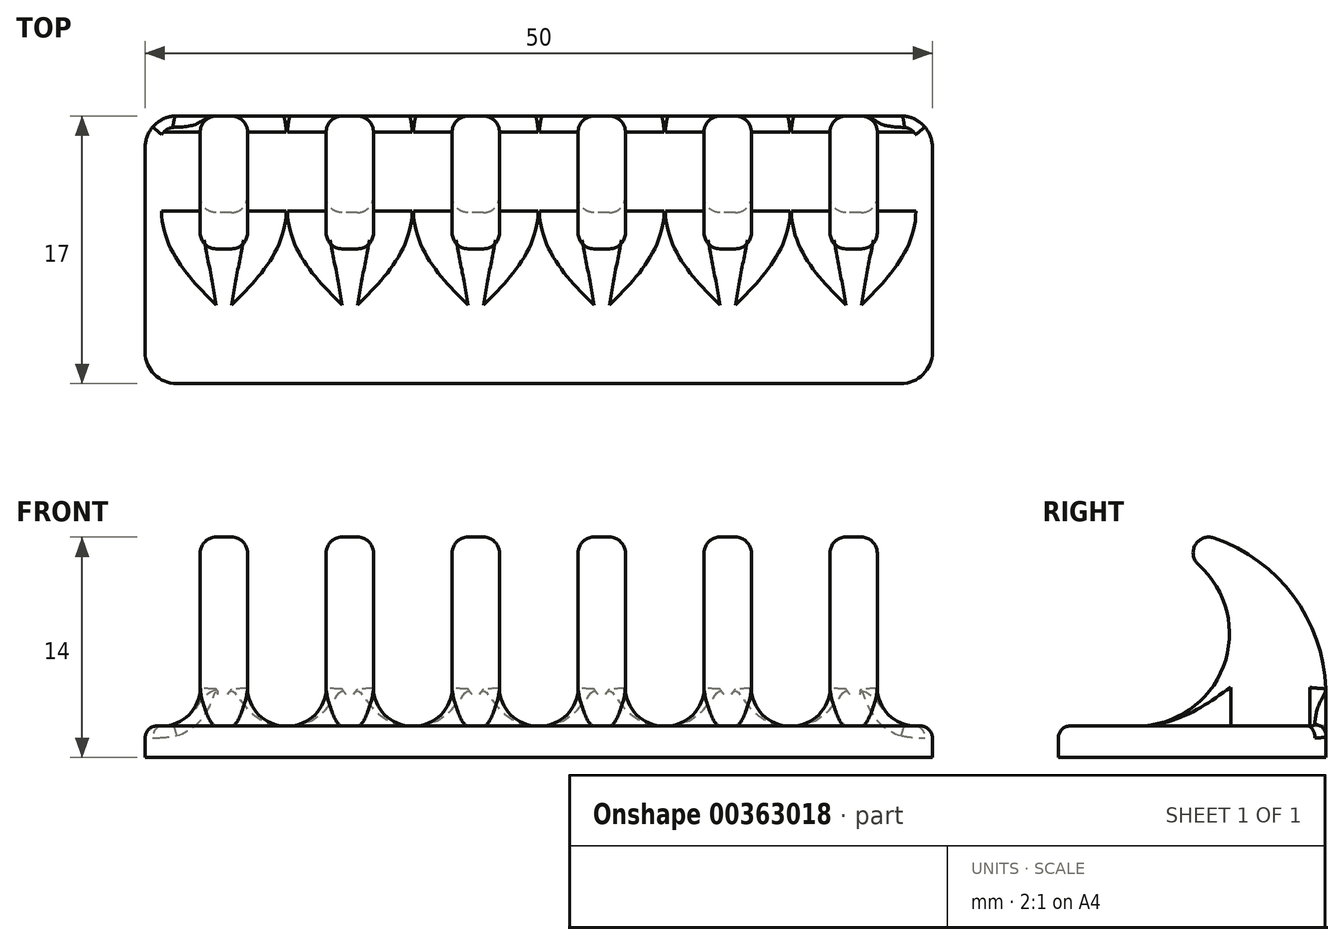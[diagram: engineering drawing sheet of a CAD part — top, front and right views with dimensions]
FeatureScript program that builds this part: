
annotation { "Feature Type Name" : "Feature", "Feature Type Description" : "" }
export const myFeature = defineFeature(function(context is Context, id is Id, definition is map)
    precondition{}
    {
        {
            var Q0;
            Q0=qCreatedBy(makeId("Top.planeOp"),FACE);
            var sketch = newSketch(context, id + "F0", { "sketchPlane" : qUnion([Q0])});
            skLineSegment(sketch, "E0.bottom", {"start": v(0, 0) * mm, "end": v(50, 0) * mm});
            skLineSegment(sketch, "E0.top", {"start": v(0, 17) * mm, "end": v(50, 17) * mm});
            skLineSegment(sketch, "E0.left", {"start": v(0, 0) * mm, "end": v(0, 17) * mm});
            skLineSegment(sketch, "E0.right", {"start": v(50, 0) * mm, "end": v(50, 17) * mm});
            skSolve(sketch);
        }
        {
            var Q0;
            Q0 = qSketchRegion(id + "F0", true);
            extrude(context, id + "F1", {"entities" : qUnion([Q0]), "depth" : 2 * mm});
        }
        {
            var Q0;
            Q0=makeQuery(id+"F1.opExtrude","CAP_FACE",FACE,{"disambiguationData":[OSD([sQuery(id+"F0.wireOp",EDGE,"E0.bottom"),sQuery(id+"F0.wireOp",EDGE,"E0.top"),sQuery(id+"F0.wireOp",EDGE,"E0.left"),sQuery(id+"F0.wireOp",EDGE,"E0.right")])],"isStart":false});
            var sketch = newSketch(context, id + "F2", { "sketchPlane" : qUnion([Q0])});
            skPoint(sketch, "E1", {"position": v(25, 17) * mm});
            skSolve(sketch);
        }
        {
            var Q0;
            Q0=makeQuery(id+"F1.opExtrude","CAP_EDGE",EDGE,{"disambiguationData":[OSD([sQuery(id+"F0.wireOp",EDGE,"E0.top")])],"isStart":false});
            cPoint(context, id + "F3", {"entities" : qUnion([Q0]), "parameter" : 0.5});
        }
        {
            var Q0;
            Q0 = qCreatedBy(id + "F3" ,VERTEX);
            var Q1;
            Q1=qCreatedBy(makeId("Right.planeOp"),FACE);
            cPlane(context, id + "F4", {"entities" : qUnion([Q0, Q1]), "cplaneType" : CPlaneType.PLANE_POINT, "offset" : 25 * mm, "width" : 150 * mm, "height" : 150 * mm});
        }
        {
            var Q0;
            Q0=qCreatedBy(id+"F4.planeOp",FACE);
            var sketch = newSketch(context, id + "F5", { "sketchPlane" : qUnion([Q0])});
            skLineSegment(sketch, "E2", {"start": v(5, 2) * mm, "end": v(17, 2) * mm});
            skArc(sketch, "E3", {"start": v(9.89, 13.95) * mm, "mid": v(8.7, 13.5) * mm, "end": v(8.9, 12.25) * mm});
            skLineSegment(sketch, "E4", {"start": v(17, 2) * mm, "end": v(17, 4) * mm});
            skArc(sketch, "E5", {"start": v(17, 4) * mm, "mid": v(15.04, 10.11) * mm, "end": v(9.89, 13.95) * mm});
            skLineSegment(sketch, "E6", {"start": v(8.9, 12.25) * mm, "end": v(8.9, 12.25) * mm});
            skArc(sketch, "E7", {"start": v(8.9, 12.25) * mm, "mid": v(10.48, 5.78) * mm, "end": v(5, 2) * mm});
            skSolve(sketch);
        }
        {
            var Q0;
            Q0 = qSketchRegion(id + "F5", true);
            extrude(context, id + "F6", {"entities" : qUnion([Q0]), "operationType" : NewBodyOperationType.ADD, "endBound" : BoundingType.SYMMETRIC, "depth" : 50 * mm});
        }
        {
            var Q0;
            Q0=makeQuery(id+"F1.opExtrude","SWEPT_FACE",FACE,{"disambiguationData":[OSD([sQuery(id+"F0.wireOp",EDGE,"E0.top")])]});
            var sketch = newSketch(context, id + "F7", { "sketchPlane" : qUnion([Q0])});
            skLineSegment(sketch, "E8.bottom", {"start": v(-27.5, 2) * mm, "end": v(-22.5, 2) * mm});
            skLineSegment(sketch, "E8.top", {"start": v(-27.5, 19) * mm, "end": v(-22.5, 19) * mm});
            skLineSegment(sketch, "E8.left", {"start": v(-27.5, 2) * mm, "end": v(-27.5, 19) * mm});
            skLineSegment(sketch, "E8.right", {"start": v(-22.5, 2) * mm, "end": v(-22.5, 19) * mm});
            skLineSegment(sketch, "E9.bottom", {"start": v(-6.5, 2) * mm, "end": v(-11.5, 2) * mm});
            skLineSegment(sketch, "E9.top", {"start": v(-6.5, 19) * mm, "end": v(-11.5, 19) * mm});
            skLineSegment(sketch, "E9.left", {"start": v(-6.5, 2) * mm, "end": v(-6.5, 19) * mm});
            skLineSegment(sketch, "E9.right", {"start": v(-11.5, 2) * mm, "end": v(-11.5, 19) * mm});
            skPoint(sketch, "E10", {"position": v(-9, 19) * mm});
            skLineSegment(sketch, "E11.bottom", {"start": v(8.53, 2) * mm, "end": v(-3.5, 2) * mm});
            skLineSegment(sketch, "E11.top", {"start": v(8.53, 19) * mm, "end": v(-3.5, 19) * mm});
            skLineSegment(sketch, "E11.left", {"start": v(8.53, 2) * mm, "end": v(8.53, 19) * mm});
            skLineSegment(sketch, "E11.right", {"start": v(-3.5, 2) * mm, "end": v(-3.5, 19) * mm});
            skPoint(sketch, "E12.firstSnap0", {"position": v(-25, 2) * mm});
            skLineSegment(sketch, "E12.bottom", {"start": v(-19.5, 2) * mm, "end": v(-14.5, 2) * mm});
            skLineSegment(sketch, "E12.top", {"start": v(-19.5, 19) * mm, "end": v(-14.5, 19) * mm});
            skLineSegment(sketch, "E12.left", {"start": v(-19.5, 2) * mm, "end": v(-19.5, 19) * mm});
            skLineSegment(sketch, "E12.right", {"start": v(-14.5, 2) * mm, "end": v(-14.5, 19) * mm});
            skLineSegment(sketch, "E13", {"start": v(-25, 2) * mm, "end": v(-25, -6.71) * mm, "construction": true});
            skPoint(sketch, "E13.endSnap0", {"position": v(-25, 0) * mm});
            skLineSegment(sketch, "E14.MirrorCS", {"start": v(-38.5, 2) * mm, "end": v(-38.5, 19) * mm});
            skLineSegment(sketch, "E15.MirrorCS", {"start": v(-58.53, 2) * mm, "end": v(-46.5, 2) * mm});
            skLineSegment(sketch, "E16.MirrorCS", {"start": v(-58.53, 19) * mm, "end": v(-46.5, 19) * mm});
            skLineSegment(sketch, "E17.MirrorCS", {"start": v(-58.53, 2) * mm, "end": v(-58.53, 19) * mm});
            skLineSegment(sketch, "E18.MirrorCS", {"start": v(-46.5, 2) * mm, "end": v(-46.5, 19) * mm});
            skLineSegment(sketch, "E19.MirrorCS", {"start": v(-30.5, 19) * mm, "end": v(-35.5, 19) * mm});
            skLineSegment(sketch, "E20.MirrorCS", {"start": v(-43.5, 2) * mm, "end": v(-43.5, 19) * mm});
            skLineSegment(sketch, "E21.MirrorCS", {"start": v(-35.5, 2) * mm, "end": v(-35.5, 19) * mm});
            skLineSegment(sketch, "E22.MirrorCS", {"start": v(-30.5, 2) * mm, "end": v(-30.5, 19) * mm});
            skPoint(sketch, "E23.MirrorP", {"position": v(-41, 19) * mm});
            skLineSegment(sketch, "E24.MirrorCS", {"start": v(-43.5, 19) * mm, "end": v(-38.5, 19) * mm});
            skLineSegment(sketch, "E25.MirrorCS", {"start": v(-43.5, 2) * mm, "end": v(-38.5, 2) * mm});
            skLineSegment(sketch, "E26.MirrorCS", {"start": v(-30.5, 2) * mm, "end": v(-35.5, 2) * mm});
            skSolve(sketch);
        }
        {
            var Q0;
            Q0 = qSketchRegion(id + "F7", true);
            extrude(context, id + "F8", {"entities" : qUnion([Q0]), "operationType" : NewBodyOperationType.REMOVE, "oppositeDirection" : true, "depth" : 25 * mm});
        }
        {
            var Q0;
            Q0=makeQuery(id+"F6.opExtrude","CAP_EDGE",EDGE,{"disambiguationData":[OSD([sQuery(id+"F5.wireOp",EDGE,"E5")])],"isStart":true});
            var Q1;
            Q1=makeQuery(id+"F8.boolean.opBoolean","INTERSECT",EDGE,{"derivedFrom":[makeQuery(id+"F6.opExtrude","SWEPT_FACE",FACE,{"disambiguationData":[OSD([sQuery(id+"F5.wireOp",EDGE,"E5")])]}),makeQuery(id+"F8.opExtrude","SWEPT_FACE",FACE,{"disambiguationData":[OSD([sQuery(id+"F7.wireOp",EDGE,"E8.right")])]})]});
            var Q2;
            Q2=makeQuery(id+"F8.boolean.opBoolean","INTERSECT",EDGE,{"derivedFrom":[makeQuery(id+"F6.opExtrude","SWEPT_FACE",FACE,{"disambiguationData":[OSD([sQuery(id+"F5.wireOp",EDGE,"E5")])]}),makeQuery(id+"F8.opExtrude","SWEPT_FACE",FACE,{"disambiguationData":[OSD([sQuery(id+"F7.wireOp",EDGE,"E12.right")])]})]});
            var Q3;
            Q3=makeQuery(id+"F8.boolean.opBoolean","INTERSECT",EDGE,{"derivedFrom":[makeQuery(id+"F6.opExtrude","SWEPT_FACE",FACE,{"disambiguationData":[OSD([sQuery(id+"F5.wireOp",EDGE,"E5")])]}),makeQuery(id+"F8.opExtrude","SWEPT_FACE",FACE,{"disambiguationData":[OSD([sQuery(id+"F7.wireOp",EDGE,"E9.left")])]})]});
            var Q4;
            Q4=makeQuery(id+"F8.boolean.opBoolean","INTERSECT",EDGE,{"derivedFrom":[makeQuery(id+"F6.opExtrude","SWEPT_FACE",FACE,{"disambiguationData":[OSD([sQuery(id+"F5.wireOp",EDGE,"E5")])]}),makeQuery(id+"F8.opExtrude","SWEPT_FACE",FACE,{"disambiguationData":[OSD([sQuery(id+"F7.wireOp",EDGE,"E22.MirrorCS")])]})]});
            var Q5;
            Q5=makeQuery(id+"F8.boolean.opBoolean","INTERSECT",EDGE,{"derivedFrom":[makeQuery(id+"F6.opExtrude","SWEPT_FACE",FACE,{"disambiguationData":[OSD([sQuery(id+"F5.wireOp",EDGE,"E5")])]}),makeQuery(id+"F8.opExtrude","SWEPT_FACE",FACE,{"disambiguationData":[OSD([sQuery(id+"F7.wireOp",EDGE,"E14.MirrorCS")])]})]});
            var Q6;
            Q6=makeQuery(id+"F8.boolean.opBoolean","INTERSECT",EDGE,{"derivedFrom":[makeQuery(id+"F6.opExtrude","SWEPT_FACE",FACE,{"disambiguationData":[OSD([sQuery(id+"F5.wireOp",EDGE,"E5")])]}),makeQuery(id+"F8.opExtrude","SWEPT_FACE",FACE,{"disambiguationData":[OSD([sQuery(id+"F7.wireOp",EDGE,"E18.MirrorCS")])]})]});
            fillet(context, id + "F9", {"entities" : qUnion([Q0, Q1, Q2, Q3, Q4, Q5, Q6]), "radius" : 1 * mm, "tangentPropagation" : true, "allowEdgeOverflow" : false});
        }
        {
            var Q0;
            Q0=makeQuery(id+"F6.opExtrude","CAP_EDGE",EDGE,{"disambiguationData":[OSD([sQuery(id+"F5.wireOp",EDGE,"E5")])],"isStart":false});
            var Q1;
            Q1=makeQuery(id+"F8.boolean.opBoolean","INTERSECT",EDGE,{"derivedFrom":[makeQuery(id+"F6.opExtrude","SWEPT_FACE",FACE,{"disambiguationData":[OSD([sQuery(id+"F5.wireOp",EDGE,"E5")])]}),makeQuery(id+"F8.opExtrude","SWEPT_FACE",FACE,{"disambiguationData":[OSD([sQuery(id+"F7.wireOp",EDGE,"E8.left")])]})]});
            var Q2;
            Q2=makeQuery(id+"F8.boolean.opBoolean","INTERSECT",EDGE,{"derivedFrom":[makeQuery(id+"F6.opExtrude","SWEPT_FACE",FACE,{"disambiguationData":[OSD([sQuery(id+"F5.wireOp",EDGE,"E5")])]}),makeQuery(id+"F8.opExtrude","SWEPT_FACE",FACE,{"disambiguationData":[OSD([sQuery(id+"F7.wireOp",EDGE,"E20.MirrorCS")])]})]});
            var Q3;
            Q3=makeQuery(id+"F8.boolean.opBoolean","INTERSECT",EDGE,{"derivedFrom":[makeQuery(id+"F6.opExtrude","SWEPT_FACE",FACE,{"disambiguationData":[OSD([sQuery(id+"F5.wireOp",EDGE,"E5")])]}),makeQuery(id+"F8.opExtrude","SWEPT_FACE",FACE,{"disambiguationData":[OSD([sQuery(id+"F7.wireOp",EDGE,"E21.MirrorCS")])]})]});
            var Q4;
            Q4=makeQuery(id+"F8.boolean.opBoolean","INTERSECT",EDGE,{"derivedFrom":[makeQuery(id+"F6.opExtrude","SWEPT_FACE",FACE,{"disambiguationData":[OSD([sQuery(id+"F5.wireOp",EDGE,"E5")])]}),makeQuery(id+"F8.opExtrude","SWEPT_FACE",FACE,{"disambiguationData":[OSD([sQuery(id+"F7.wireOp",EDGE,"E12.left")])]})]});
            var Q5;
            Q5=makeQuery(id+"F8.boolean.opBoolean","INTERSECT",EDGE,{"derivedFrom":[makeQuery(id+"F6.opExtrude","SWEPT_FACE",FACE,{"disambiguationData":[OSD([sQuery(id+"F5.wireOp",EDGE,"E5")])]}),makeQuery(id+"F8.opExtrude","SWEPT_FACE",FACE,{"disambiguationData":[OSD([sQuery(id+"F7.wireOp",EDGE,"E9.right")])]})]});
            var Q6;
            Q6=makeQuery(id+"F8.boolean.opBoolean","INTERSECT",EDGE,{"derivedFrom":[makeQuery(id+"F6.opExtrude","SWEPT_FACE",FACE,{"disambiguationData":[OSD([sQuery(id+"F5.wireOp",EDGE,"E5")])]}),makeQuery(id+"F8.opExtrude","SWEPT_FACE",FACE,{"disambiguationData":[OSD([sQuery(id+"F7.wireOp",EDGE,"E11.right")])]})]});
            fillet(context, id + "F10", {"entities" : qUnion([Q0, Q1, Q2, Q3, Q4, Q5, Q6]), "radius" : 1 * mm, "tangentPropagation" : true, "allowEdgeOverflow" : false});
        }
        {
            var Q0;
            Q0=makeQuery(id+"F6.opExtrude","CAP_EDGE",EDGE,{"disambiguationData":[OSD([sQuery(id+"F5.wireOp",EDGE,"E2")])],"isStart":false});
            var Q1;
            Q1=makeQuery(id+"F8.boolean.opBoolean","COPY",EDGE,{"derivedFrom":makeQuery(id+"F8.opExtrude","SWEPT_EDGE",EDGE,{"disambiguationData":[OSD([sQuery(id+"F7.wireOp",EDGE,"E8.bottom"),sQuery(id+"F7.wireOp",EDGE,"E8.left")])]})});
            var Q2;
            Q2=makeQuery(id+"F8.boolean.opBoolean","COPY",EDGE,{"derivedFrom":makeQuery(id+"F8.opExtrude","SWEPT_EDGE",EDGE,{"disambiguationData":[OSD([sQuery(id+"F7.wireOp",EDGE,"E20.MirrorCS"),sQuery(id+"F7.wireOp",EDGE,"E25.MirrorCS")])]})});
            var Q3;
            Q3=makeQuery(id+"F8.boolean.opBoolean","COPY",EDGE,{"derivedFrom":makeQuery(id+"F8.opExtrude","SWEPT_EDGE",EDGE,{"disambiguationData":[OSD([sQuery(id+"F7.wireOp",EDGE,"E21.MirrorCS"),sQuery(id+"F7.wireOp",EDGE,"E26.MirrorCS")])]})});
            var Q4;
            Q4=makeQuery(id+"F8.boolean.opBoolean","COPY",EDGE,{"derivedFrom":makeQuery(id+"F8.opExtrude","SWEPT_EDGE",EDGE,{"disambiguationData":[OSD([sQuery(id+"F7.wireOp",EDGE,"E12.bottom"),sQuery(id+"F7.wireOp",EDGE,"E12.left")])]})});
            var Q5;
            Q5=makeQuery(id+"F8.boolean.opBoolean","COPY",EDGE,{"derivedFrom":makeQuery(id+"F8.opExtrude","SWEPT_EDGE",EDGE,{"disambiguationData":[OSD([sQuery(id+"F7.wireOp",EDGE,"E9.bottom"),sQuery(id+"F7.wireOp",EDGE,"E9.right")])]})});
            var Q6;
            Q6=makeQuery(id+"F8.boolean.opBoolean","COPY",EDGE,{"derivedFrom":makeQuery(id+"F8.opExtrude","SWEPT_EDGE",EDGE,{"disambiguationData":[OSD([sQuery(id+"F7.wireOp",EDGE,"E11.bottom"),sQuery(id+"F7.wireOp",EDGE,"E11.right")])]})});
            fillet(context, id + "F11", {"entities" : qUnion([Q0, Q1, Q2, Q3, Q4, Q5, Q6]), "radius" : 2.45 * mm, "tangentPropagation" : true, "allowEdgeOverflow" : false});
        }
        {
            var Q0;
            Q0=makeQuery(id+"F8.boolean.opBoolean","COPY",EDGE,{"derivedFrom":makeQuery(id+"F8.opExtrude","SWEPT_EDGE",EDGE,{"disambiguationData":[OSD([sQuery(id+"F7.wireOp",EDGE,"E8.bottom"),sQuery(id+"F7.wireOp",EDGE,"E8.right")])]})});
            var Q1;
            Q1=makeQuery(id+"F6.opExtrude","CAP_EDGE",EDGE,{"disambiguationData":[OSD([sQuery(id+"F5.wireOp",EDGE,"E2")])],"isStart":true});
            var Q2;
            Q2=makeQuery(id+"F8.boolean.opBoolean","COPY",EDGE,{"derivedFrom":makeQuery(id+"F8.opExtrude","SWEPT_EDGE",EDGE,{"disambiguationData":[OSD([sQuery(id+"F7.wireOp",EDGE,"E9.bottom"),sQuery(id+"F7.wireOp",EDGE,"E9.left")])]})});
            var Q3;
            Q3=makeQuery(id+"F8.boolean.opBoolean","COPY",EDGE,{"derivedFrom":makeQuery(id+"F8.opExtrude","SWEPT_EDGE",EDGE,{"disambiguationData":[OSD([sQuery(id+"F7.wireOp",EDGE,"E12.bottom"),sQuery(id+"F7.wireOp",EDGE,"E12.right")])]})});
            var Q4;
            Q4=makeQuery(id+"F8.boolean.opBoolean","COPY",EDGE,{"derivedFrom":makeQuery(id+"F8.opExtrude","SWEPT_EDGE",EDGE,{"disambiguationData":[OSD([sQuery(id+"F7.wireOp",EDGE,"E22.MirrorCS"),sQuery(id+"F7.wireOp",EDGE,"E26.MirrorCS")])]})});
            var Q5;
            Q5=makeQuery(id+"F8.boolean.opBoolean","COPY",EDGE,{"derivedFrom":makeQuery(id+"F8.opExtrude","SWEPT_EDGE",EDGE,{"disambiguationData":[OSD([sQuery(id+"F7.wireOp",EDGE,"E14.MirrorCS"),sQuery(id+"F7.wireOp",EDGE,"E25.MirrorCS")])]})});
            var Q6;
            Q6=makeQuery(id+"F8.boolean.opBoolean","COPY",EDGE,{"derivedFrom":makeQuery(id+"F8.opExtrude","SWEPT_EDGE",EDGE,{"disambiguationData":[OSD([sQuery(id+"F7.wireOp",EDGE,"E15.MirrorCS"),sQuery(id+"F7.wireOp",EDGE,"E18.MirrorCS")])]})});
            fillet(context, id + "F12", {"entities" : qUnion([Q0, Q1, Q2, Q3, Q4, Q5, Q6]), "radius" : 2.45 * mm, "tangentPropagation" : true, "allowEdgeOverflow" : false});
        }
        {
            var Q0;
            Q0=makeQuery(id+"F1.opExtrude","SWEPT_EDGE",EDGE,{"disambiguationData":[OSD([sQuery(id+"F0.wireOp",EDGE,"E0.bottom"),sQuery(id+"F0.wireOp",EDGE,"E0.left")])]});
            var Q1;
            Q1=makeQuery(id+"F1.opExtrude","SWEPT_EDGE",EDGE,{"disambiguationData":[OSD([sQuery(id+"F0.wireOp",EDGE,"E0.bottom"),sQuery(id+"F0.wireOp",EDGE,"E0.right")])]});
            var Q2;
            Q2=makeQuery(id+"F6.boolean.opBoolean","MERGE",EDGE,{"derivedFrom":[makeQuery(id+"F1.opExtrude","SWEPT_EDGE",EDGE,{"disambiguationData":[OSD([sQuery(id+"F0.wireOp",EDGE,"E0.top"),sQuery(id+"F0.wireOp",EDGE,"E0.right")])]}),makeQuery(id+"F6.opExtrude","CAP_EDGE",EDGE,{"disambiguationData":[OSD([sQuery(id+"F5.wireOp",EDGE,"E4")])],"isStart":false})]});
            var Q3;
            Q3=makeQuery(id+"F6.boolean.opBoolean","MERGE",EDGE,{"derivedFrom":[makeQuery(id+"F1.opExtrude","SWEPT_EDGE",EDGE,{"disambiguationData":[OSD([sQuery(id+"F0.wireOp",EDGE,"E0.top"),sQuery(id+"F0.wireOp",EDGE,"E0.left")])]}),makeQuery(id+"F6.opExtrude","CAP_EDGE",EDGE,{"disambiguationData":[OSD([sQuery(id+"F5.wireOp",EDGE,"E4")])],"isStart":true})]});
            fillet(context, id + "F13", {"entities" : qUnion([Q0, Q1, Q2, Q3]), "radius" : 2 * mm, "tangentPropagation" : true, "allowEdgeOverflow" : false});
        }
        {
            var Q0;
            Q0=makeQuery(id+"F8.boolean.opBoolean","INTERSECT",EDGE,{"derivedFrom":[makeQuery(id+"F6.boolean.opBoolean","MERGE",FACE,{"derivedFrom":[makeQuery(id+"F1.opExtrude","SWEPT_FACE",FACE,{"disambiguationData":[OSD([sQuery(id+"F0.wireOp",EDGE,"E0.left")])]}),makeQuery(id+"F6.opExtrude","CAP_FACE",FACE,{"disambiguationData":[OSD([sQuery(id+"F5.wireOp",EDGE,"E2"),sQuery(id+"F5.wireOp",EDGE,"E3"),sQuery(id+"F5.wireOp",EDGE,"E4"),sQuery(id+"F5.wireOp",EDGE,"E5"),sQuery(id+"F5.wireOp",EDGE,"E7")])],"isStart":true})]}),makeQuery(id+"F8.opExtrude","SWEPT_FACE",FACE,{"disambiguationData":[OSD([sQuery(id+"F7.wireOp",EDGE,"E11.bottom")])]})]});
            fillet(context, id + "F14", {"entities" : qUnion([Q0]), "radius" : .75 * mm, "tangentPropagation" : true, "allowEdgeOverflow" : false});
        }
    });
